AUTODESK INVENTOR PART (.ipt)
format: ipt  version: 2023 (Build 270158000, 158)  size: 164,864 bytes
history: native  units: mm
features: extrude x2, sketch x1
ambient origin geometry x8: Origin, YZ Plane, XZ Plane, XY Plane, X Axis, Y Axis, Z Axis, Center Point
bodies: Solid1 (feature_tree), body (feature_tree)
feature tree (3):
  sketch  "Sketch6"  dims[d5=42.3mm d6=42.3mm d7=2.0mm d8=2.0mm d9=2.0mm d10=2.0mm d11=2.0mm d12=2.0mm d13=2.0mm d14=2.0mm d15=3.0mm d16=3.0mm d17=3.0mm d18=3.0mm d19=5.0mm d20=34.0mm d21=0.0mm d22=24.0mm d23=0.0mm]
  extrude  "Extrusion1"  Depth=42.3mm
  extrude  "Extrusion2"  Depth=24.0mm
